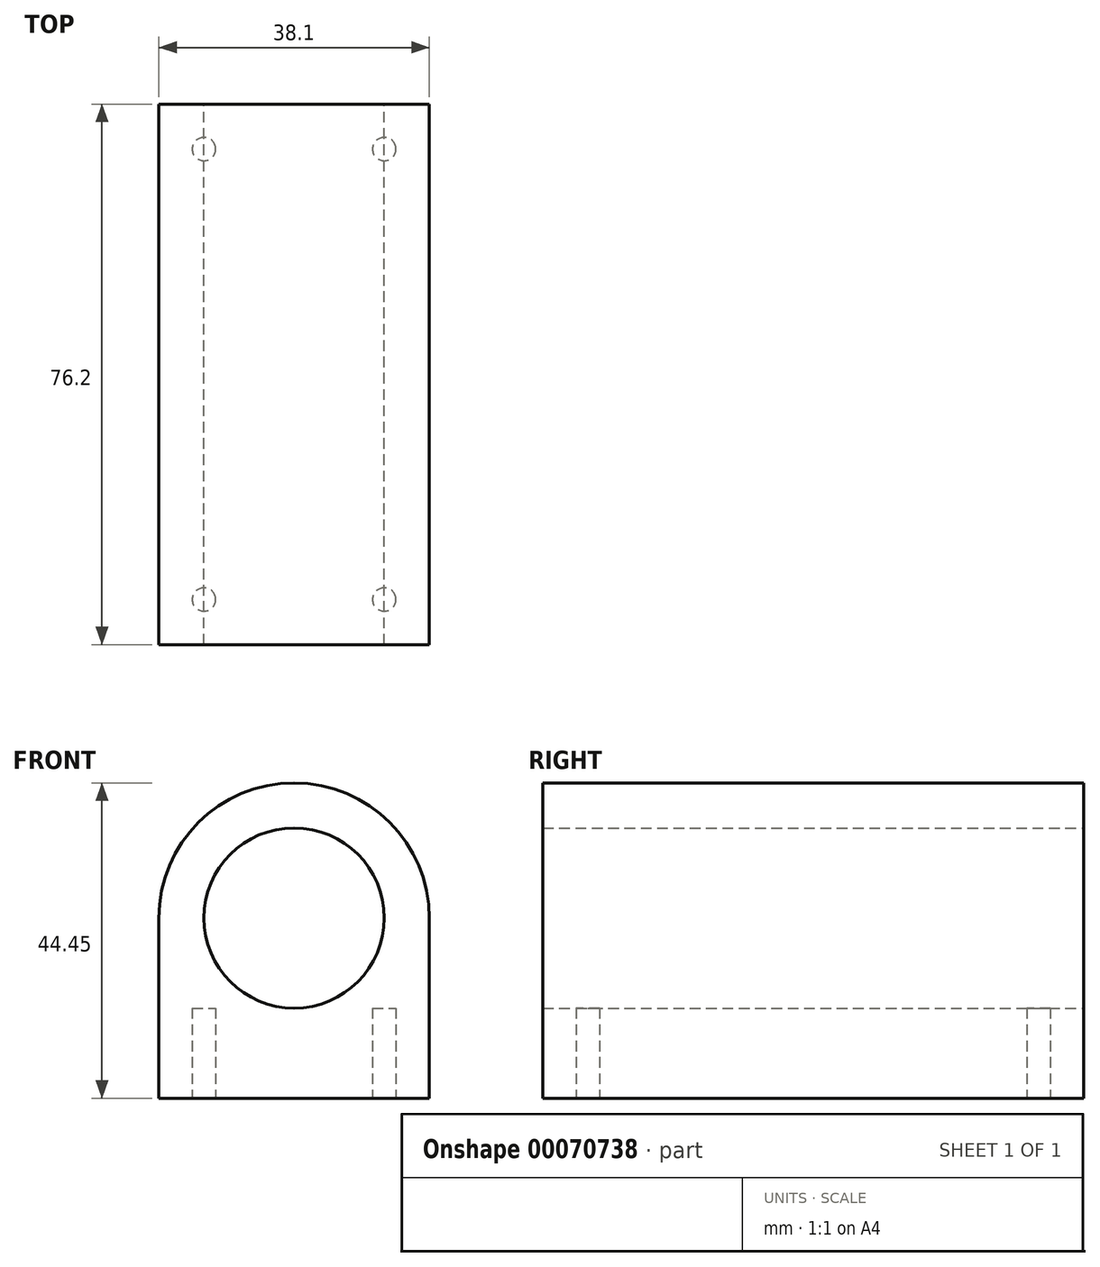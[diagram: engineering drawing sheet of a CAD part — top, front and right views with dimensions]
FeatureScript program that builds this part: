
annotation { "Feature Type Name" : "Feature", "Feature Type Description" : "" }
export const myFeature = defineFeature(function(context is Context, id is Id, definition is map)
    precondition{}
    {
        {
            var Q0;
            Q0=qCreatedBy(makeId("Front.planeOp"),FACE);
            var sketch = newSketch(context, id + "F0", { "sketchPlane" : qUnion([Q0])});
            skLineSegment(sketch, "E0.bottom", {"start": v(0, 0) * mm, "end": v(38.1, 0) * mm});
            skLineSegment(sketch, "E0.left", {"start": v(0, 0) * mm, "end": v(0, 25.4) * mm});
            skLineSegment(sketch, "E0.right", {"start": v(38.1, 0) * mm, "end": v(38.1, 25.4) * mm});
            skArc(sketch, "E1", {"start": v(38.1, 25.4) * mm, "mid": v(19.05, 44.45) * mm, "end": v(0, 25.4) * mm});
            skCircle(sketch, "E2", {"center": v(19.05, 25.4) * mm, "radius": 12.7 * mm});
            skSolve(sketch);
        }
        {
            var Q0;
            Q0=makeQuery(id+"F0.imprint","IMPRINT",FACE,{"disambiguationData":[TD([[makeQuery(id+"F0.imprint","IMPRINT",EDGE,{"derivedFrom":sQuery(id+"F0.wireOp",EDGE,"E0.bottom")}),1.0]])]});
            extrude(context, id + "F1", {"entities" : qUnion([Q0]), "depth" : 76.2 * mm});
        }
        {
            var Q0;
            Q0=makeQuery(id+"F1.opExtrude","SWEPT_FACE",FACE,{"disambiguationData":[OSD([sQuery(id+"F0.wireOp",EDGE,"E0.bottom")])]});
            var sketch = newSketch(context, id + "F2", { "sketchPlane" : qUnion([Q0])});
            skCircle(sketch, "E3", {"center": v(6.35, 69.85) * mm, "radius": 1.65 * mm});
            skCircle(sketch, "E4", {"center": v(31.75, 69.85) * mm, "radius": 1.65 * mm});
            skCircle(sketch, "E5", {"center": v(6.35, 6.35) * mm, "radius": 1.65 * mm});
            skCircle(sketch, "E6", {"center": v(31.75, 6.35) * mm, "radius": 1.65 * mm});
            skSolve(sketch);
        }
        {
            var Q0;
            Q0=makeQuery(id+"F2.imprint","IMPRINT",FACE,{"disambiguationData":[TD([[makeQuery(id+"F2.imprint","IMPRINT",EDGE,{"derivedFrom":sQuery(id+"F2.wireOp",EDGE,"E3")}),1.0]])]});
            var Q1;
            Q1=makeQuery(id+"F2.imprint","IMPRINT",FACE,{"disambiguationData":[TD([[makeQuery(id+"F2.imprint","IMPRINT",EDGE,{"derivedFrom":sQuery(id+"F2.wireOp",EDGE,"E5")}),1.0]])]});
            var Q2;
            Q2=makeQuery(id+"F2.imprint","IMPRINT",FACE,{"disambiguationData":[TD([[makeQuery(id+"F2.imprint","IMPRINT",EDGE,{"derivedFrom":sQuery(id+"F2.wireOp",EDGE,"E6")}),1.0]])]});
            var Q3;
            Q3=makeQuery(id+"F2.imprint","IMPRINT",FACE,{"disambiguationData":[TD([[makeQuery(id+"F2.imprint","IMPRINT",EDGE,{"derivedFrom":sQuery(id+"F2.wireOp",EDGE,"E4")}),1.0]])]});
            extrude(context, id + "F3", {"entities" : qUnion([Q0, Q1, Q2, Q3]), "operationType" : NewBodyOperationType.REMOVE, "oppositeDirection" : true, "depth" : 12.7 * mm});
        }
    });
